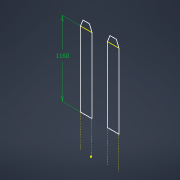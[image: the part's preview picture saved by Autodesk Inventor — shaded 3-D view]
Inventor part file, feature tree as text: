
AUTODESK INVENTOR PART (.ipt)
format: ipt  version: 2022 (Build 260153000, 153)  size: 82,432 bytes
history: native  units: mm
features: reference x12, other x3, sketch x1
ambient origin geometry x8: Origin, YZ Plane, XZ Plane, XY Plane, X Axis, Y Axis, Z Axis, Center Point
feature tree (16):
  sketch  "Sketch2"  dims[d1=1160.0mm]
  reference  "Reference13"
  reference  "Reference14"
  reference  "Reference15"
  reference  "Reference16"
  reference  "Reference17"
  reference  "Reference18"
  reference  "Reference19"
  reference  "Reference20"
  reference  "Reference21"
  reference  "Reference22"
  reference  "Reference23"
  reference  "Reference24"
  other  "RobotPallet.iam"
  other  "EstructuraInferior:1"
  other  "EstructuraInferior_Esqueleto:1"
